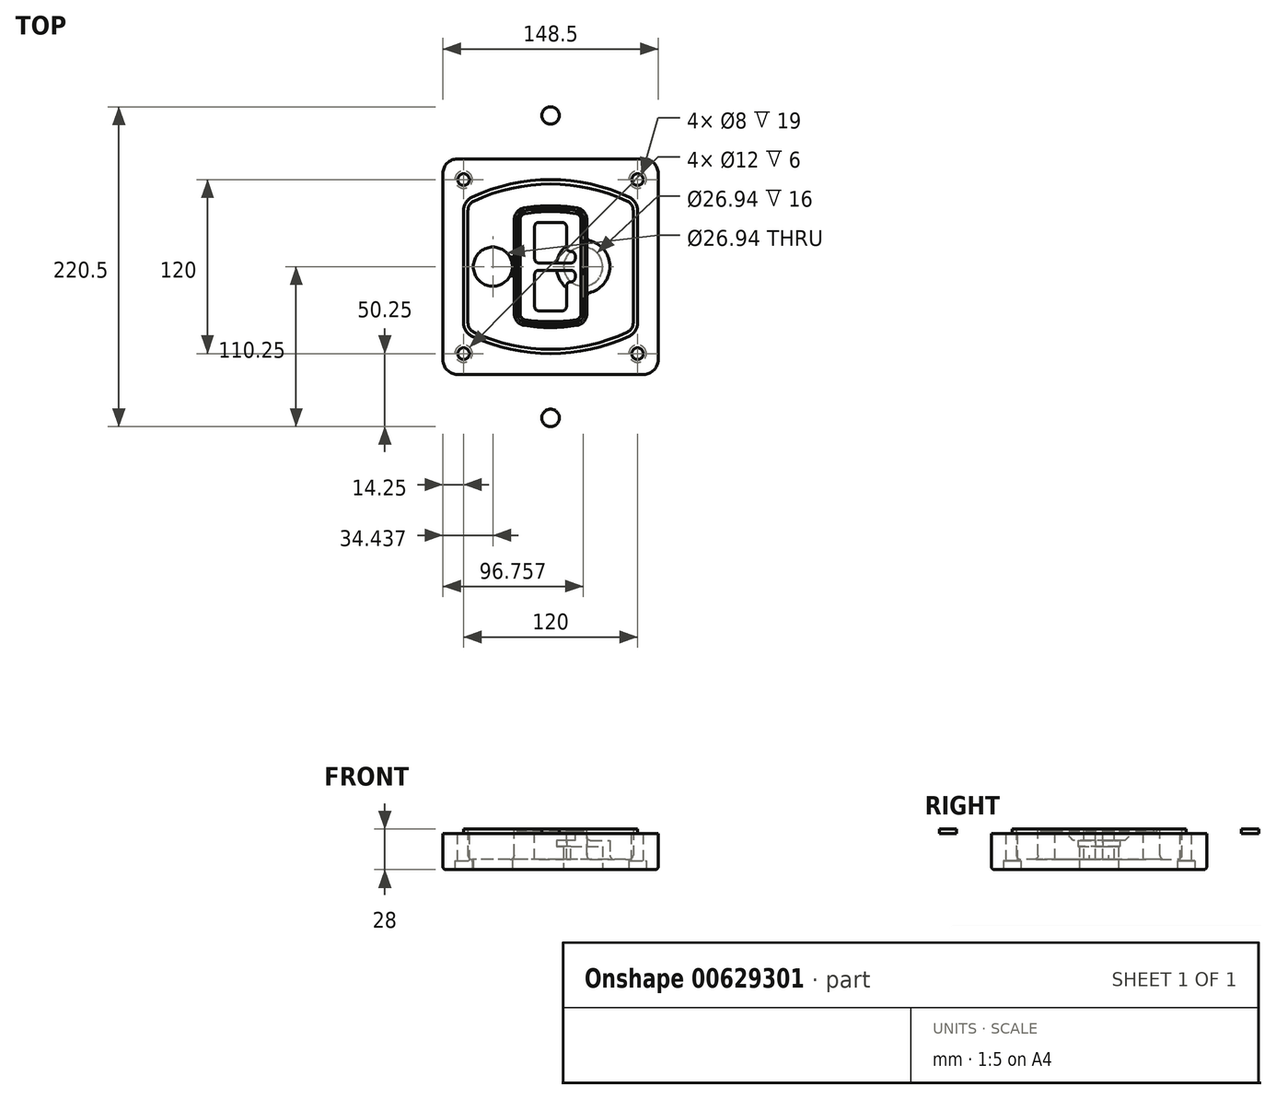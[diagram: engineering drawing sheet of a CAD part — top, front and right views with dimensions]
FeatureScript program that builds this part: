
annotation { "Feature Type Name" : "Feature", "Feature Type Description" : "" }
export const myFeature = defineFeature(function(context is Context, id is Id, definition is map)
    precondition{}
    {
        {
            var Q0;
            Q0=qCreatedBy(makeId("Top.planeOp"),FACE);
            var sketch = newSketch(context, id + "F0", { "sketchPlane" : qUnion([Q0])});
            skPoint(sketch, "E0.rect.middle", {"position": v(0, 0) * mm});
            skLineSegment(sketch, "E1.bottom", {"start": v(-64.25, -74.25) * mm, "end": v(64.25, -74.25) * mm});
            skLineSegment(sketch, "E1.top", {"start": v(-64.25, 74.25) * mm, "end": v(64.25, 74.25) * mm});
            skLineSegment(sketch, "E1.left", {"start": v(-74.25, -64.25) * mm, "end": v(-74.25, 64.25) * mm});
            skLineSegment(sketch, "E1.right", {"start": v(74.25, -64.25) * mm, "end": v(74.25, 64.25) * mm});
            skLineSegment(sketch, "E2", {"start": v(-74.25, 74.25) * mm, "end": v(74.25, -74.25) * mm, "construction": true});
            skLineSegment(sketch, "E3", {"start": v(74.25, 74.25) * mm, "end": v(-74.25, -74.25) * mm, "construction": true});
            skCircle(sketch, "E4", {"center": v(-60, 60) * mm, "radius": 4 * mm});
            skCircle(sketch, "E5", {"center": v(60, 60) * mm, "radius": 4 * mm});
            skCircle(sketch, "E6", {"center": v(60, -60) * mm, "radius": 4 * mm});
            skCircle(sketch, "E7", {"center": v(-60, -60) * mm, "radius": 4 * mm});
            skLineSegment(sketch, "E8", {"start": v(-60, 60) * mm, "end": v(60, 60) * mm, "construction": true});
            skLineSegment(sketch, "E9", {"start": v(60, 60) * mm, "end": v(60, -60) * mm, "construction": true});
            skLineSegment(sketch, "E10", {"start": v(60, -60) * mm, "end": v(-60, -60) * mm, "construction": true});
            skLineSegment(sketch, "E11", {"start": v(-60, -60) * mm, "end": v(-60, 60) * mm, "construction": true});
            skLineSegment(sketch, "E12", {"start": v(-60, 38.83) * mm, "end": v(-60, -38.83) * mm});
            skLineSegment(sketch, "E13", {"start": v(60, 38.83) * mm, "end": v(60, -38.83) * mm});
            skArc(sketch, "E14", {"start": v(54.26, 47.88) * mm, "mid": v(0, 60) * mm, "end": v(-54.26, 47.88) * mm});
            skArc(sketch, "E15", {"start": v(-54.26, -47.88) * mm, "mid": v(0, -60) * mm, "end": v(54.26, -47.88) * mm});
            skLineSegment(sketch, "E16", {"start": v(-60, 0) * mm, "end": v(60, 0) * mm, "construction": true});
            skPoint(sketch, "E17.visualSharp", {"position": v(-60, -45) * mm});
            skArc(sketch, "E17.filletArc", {"start": v(-60, -38.83) * mm, "mid": v(-58.44, -44.2) * mm, "end": v(-54.26, -47.88) * mm});
            skPoint(sketch, "E18.visualSharp", {"position": v(-60, 45) * mm});
            skArc(sketch, "E18.filletArc", {"start": v(-54.26, 47.88) * mm, "mid": v(-58.44, 44.2) * mm, "end": v(-60, 38.83) * mm});
            skPoint(sketch, "E19.visualSharp", {"position": v(60, 45) * mm});
            skArc(sketch, "E19.filletArc", {"start": v(60, 38.83) * mm, "mid": v(58.44, 44.2) * mm, "end": v(54.26, 47.88) * mm});
            skPoint(sketch, "E20.visualSharp", {"position": v(60, -45) * mm});
            skArc(sketch, "E20.filletArc", {"start": v(54.26, -47.88) * mm, "mid": v(58.44, -44.2) * mm, "end": v(60, -38.83) * mm});
            skPoint(sketch, "E21.visualSharp", {"position": v(-74.25, 74.25) * mm});
            skArc(sketch, "E21.filletArc", {"start": v(-64.25, 74.25) * mm, "mid": v(-71.32, 71.32) * mm, "end": v(-74.25, 64.25) * mm});
            skPoint(sketch, "E22.visualSharp", {"position": v(74.25, 74.25) * mm});
            skArc(sketch, "E22.filletArc", {"start": v(74.25, 64.25) * mm, "mid": v(71.32, 71.32) * mm, "end": v(64.25, 74.25) * mm});
            skPoint(sketch, "E23.visualSharp", {"position": v(74.25, -74.25) * mm});
            skArc(sketch, "E23.filletArc", {"start": v(64.25, -74.25) * mm, "mid": v(71.32, -71.32) * mm, "end": v(74.25, -64.25) * mm});
            skPoint(sketch, "E24.visualSharp", {"position": v(-74.25, -74.25) * mm});
            skArc(sketch, "E24.filletArc", {"start": v(-74.25, -64.25) * mm, "mid": v(-71.32, -71.32) * mm, "end": v(-64.25, -74.25) * mm});
            skArc(sketch, "E25.0", {"start": v(57, 38.83) * mm, "mid": v(55.9, 42.58) * mm, "end": v(52.98, 45.17) * mm});
            skLineSegment(sketch, "E25.1", {"start": v(57, 38.83) * mm, "end": v(57, -38.83) * mm});
            skArc(sketch, "E25.2", {"start": v(52.98, -45.17) * mm, "mid": v(55.9, -42.58) * mm, "end": v(57, -38.83) * mm});
            skArc(sketch, "E25.3", {"start": v(-52.98, -45.17) * mm, "mid": v(0, -57) * mm, "end": v(52.98, -45.17) * mm});
            skArc(sketch, "E25.4", {"start": v(-57, -38.83) * mm, "mid": v(-55.9, -42.58) * mm, "end": v(-52.98, -45.17) * mm});
            skArc(sketch, "E25.5", {"start": v(52.98, 45.17) * mm, "mid": v(0, 57) * mm, "end": v(-52.98, 45.17) * mm});
            skLineSegment(sketch, "E25.6", {"start": v(-57, 38.83) * mm, "end": v(-57, -38.83) * mm});
            skArc(sketch, "E25.7", {"start": v(-52.98, 45.17) * mm, "mid": v(-55.9, 42.58) * mm, "end": v(-57, 38.83) * mm});
            skArc(sketch, "E26.0", {"start": v(-55.96, 51.5) * mm, "mid": v(-61.82, 46.33) * mm, "end": v(-64, 38.83) * mm});
            skArc(sketch, "E26.1", {"start": v(55.96, 51.5) * mm, "mid": v(0, 64) * mm, "end": v(-55.96, 51.5) * mm});
            skArc(sketch, "E26.2", {"start": v(64, 38.83) * mm, "mid": v(61.82, 46.33) * mm, "end": v(55.96, 51.5) * mm});
            skLineSegment(sketch, "E26.3", {"start": v(64, 38.83) * mm, "end": v(64, -38.83) * mm});
            skArc(sketch, "E26.4", {"start": v(55.96, -51.5) * mm, "mid": v(61.82, -46.33) * mm, "end": v(64, -38.83) * mm});
            skLineSegment(sketch, "E26.5", {"start": v(-64, 38.83) * mm, "end": v(-64, -38.83) * mm});
            skArc(sketch, "E26.6", {"start": v(-55.96, -51.5) * mm, "mid": v(0, -64) * mm, "end": v(55.96, -51.5) * mm});
            skArc(sketch, "E26.7", {"start": v(-64, -38.83) * mm, "mid": v(-61.82, -46.33) * mm, "end": v(-55.96, -51.5) * mm});
            skSolve(sketch);
        }
        {
            var Q0;
            Q0=makeQuery(id+"F0.imprint","IMPRINT",FACE,{"disambiguationData":[TD([[makeQuery(id+"F0.imprint","IMPRINT",EDGE,{"derivedFrom":sQuery(id+"F0.wireOp",EDGE,"E1.bottom")}),1.0]])]});
            var Q1;
            Q1=makeQuery(id+"F0.imprint","IMPRINT",FACE,{"disambiguationData":[TD([[makeQuery(id+"F0.imprint","IMPRINT",EDGE,{"derivedFrom":sQuery(id+"F0.wireOp",EDGE,"E12")}),1.0]])]});
            var Q2;
            Q2=makeQuery(id+"F0.imprint","IMPRINT",FACE,{"disambiguationData":[TD([[makeQuery(id+"F0.imprint","IMPRINT",EDGE,{"derivedFrom":sQuery(id+"F0.wireOp",EDGE,"E25.0")}),1.0]])]});
            var Q3;
            Q3=makeQuery(id+"F0.imprint","IMPRINT",FACE,{"disambiguationData":[TD([[makeQuery(id+"F0.imprint","IMPRINT",EDGE,{"derivedFrom":sQuery(id+"F0.wireOp",EDGE,"E12")}),-1.0]])]});
            extrude(context, id + "F1", {"entities" : qUnion([Q0, Q1, Q2, Q3]), "oppositeDirection" : true, "depth" : 25 * mm});
        }
        {
            var Q0;
            Q0=makeQuery(id+"F0.imprint","IMPRINT",FACE,{"disambiguationData":[TD([[makeQuery(id+"F0.imprint","IMPRINT",EDGE,{"derivedFrom":sQuery(id+"F0.wireOp",EDGE,"E12")}),1.0]])]});
            extrude(context, id + "F2", {"entities" : qUnion([Q0]), "operationType" : NewBodyOperationType.ADD, "depth" : 3 * mm});
        }
        {
            var Q0;
            Q0=makeQuery(id+"F0.imprint","IMPRINT",FACE,{"disambiguationData":[TD([[makeQuery(id+"F0.imprint","IMPRINT",EDGE,{"derivedFrom":sQuery(id+"F0.wireOp",EDGE,"E25.0")}),1.0]])]});
            extrude(context, id + "F3", {"entities" : qUnion([Q0]), "operationType" : NewBodyOperationType.REMOVE, "oppositeDirection" : true, "depth" : 18 * mm});
        }
        {
            var Q0;
            Q0=makeQuery(id+"F2.opExtrude","CAP_FACE",FACE,{"disambiguationData":[OSD([sQuery(id+"F0.wireOp",EDGE,"E12"),sQuery(id+"F0.wireOp",EDGE,"E13"),sQuery(id+"F0.wireOp",EDGE,"E14"),sQuery(id+"F0.wireOp",EDGE,"E15"),sQuery(id+"F0.wireOp",EDGE,"E17.filletArc"),sQuery(id+"F0.wireOp",EDGE,"E18.filletArc"),sQuery(id+"F0.wireOp",EDGE,"E19.filletArc"),sQuery(id+"F0.wireOp",EDGE,"E20.filletArc"),sQuery(id+"F0.wireOp",EDGE,"E25.0"),sQuery(id+"F0.wireOp",EDGE,"E25.1"),sQuery(id+"F0.wireOp",EDGE,"E25.2"),sQuery(id+"F0.wireOp",EDGE,"E25.3"),sQuery(id+"F0.wireOp",EDGE,"E25.4"),sQuery(id+"F0.wireOp",EDGE,"E25.5"),sQuery(id+"F0.wireOp",EDGE,"E25.6"),sQuery(id+"F0.wireOp",EDGE,"E25.7")])],"isStart":false});
            var sketch = newSketch(context, id + "F4", { "sketchPlane" : qUnion([Q0])});
            skArc(sketch, "E27.0", {"start": v(-18.34, -40.45) * mm, "mid": v(0, -42) * mm, "end": v(18.34, -40.45) * mm});
            skArc(sketch, "E28.0", {"start": v(18.34, 40.45) * mm, "mid": v(0, 42) * mm, "end": v(-18.34, 40.45) * mm});
            skLineSegment(sketch, "E29", {"start": v(-25, 32.57) * mm, "end": v(-25, -32.57) * mm});
            skLineSegment(sketch, "E30", {"start": v(25, 32.57) * mm, "end": v(25, -32.57) * mm});
            skLineSegment(sketch, "E31", {"start": v(-25, 39.1) * mm, "end": v(25, 39.1) * mm, "construction": true});
            skLineSegment(sketch, "E32", {"start": v(-25, -39.1) * mm, "end": v(25, -39.1) * mm, "construction": true});
            skPoint(sketch, "E33.visualSharp", {"position": v(-25, 39.1) * mm});
            skArc(sketch, "E33.filletArc", {"start": v(-18.34, 40.45) * mm, "mid": v(-23.11, 37.73) * mm, "end": v(-25, 32.57) * mm});
            skPoint(sketch, "E34.visualSharp", {"position": v(25, 39.1) * mm});
            skArc(sketch, "E34.filletArc", {"start": v(25, 32.57) * mm, "mid": v(23.11, 37.73) * mm, "end": v(18.34, 40.45) * mm});
            skPoint(sketch, "E35.visualSharp", {"position": v(25, -39.1) * mm});
            skArc(sketch, "E35.filletArc", {"start": v(18.34, -40.45) * mm, "mid": v(23.11, -37.73) * mm, "end": v(25, -32.57) * mm});
            skPoint(sketch, "E36.visualSharp", {"position": v(-25, -39.1) * mm});
            skArc(sketch, "E36.filletArc", {"start": v(-25, -32.57) * mm, "mid": v(-23.11, -37.73) * mm, "end": v(-18.34, -40.45) * mm});
            skArc(sketch, "E37.0", {"start": v(52.98, 45.17) * mm, "mid": v(0, 57) * mm, "end": v(-52.98, 45.17) * mm});
            skArc(sketch, "E37.1", {"start": v(-52.98, 45.17) * mm, "mid": v(-55.9, 42.58) * mm, "end": v(-57, 38.83) * mm});
            skLineSegment(sketch, "E37.2", {"start": v(-57, 38.83) * mm, "end": v(-57, -38.83) * mm});
            skArc(sketch, "E37.3", {"start": v(-57, -38.83) * mm, "mid": v(-55.9, -42.58) * mm, "end": v(-52.98, -45.17) * mm});
            skArc(sketch, "E37.4", {"start": v(-52.98, -45.17) * mm, "mid": v(0, -57) * mm, "end": v(52.98, -45.17) * mm});
            skArc(sketch, "E37.5", {"start": v(52.98, -45.17) * mm, "mid": v(55.9, -42.58) * mm, "end": v(57, -38.83) * mm});
            skLineSegment(sketch, "E37.6", {"start": v(57, 38.83) * mm, "end": v(57, -38.83) * mm});
            skArc(sketch, "E37.7", {"start": v(57, 38.83) * mm, "mid": v(55.9, 42.58) * mm, "end": v(52.98, 45.17) * mm});
            skLineSegment(sketch, "E38.0", {"start": v(23, 32.57) * mm, "end": v(23, -32.57) * mm});
            skArc(sketch, "E38.1", {"start": v(18, -38.48) * mm, "mid": v(21.58, -36.44) * mm, "end": v(23, -32.57) * mm});
            skArc(sketch, "E38.2", {"start": v(-18, -38.48) * mm, "mid": v(0, -40) * mm, "end": v(18, -38.48) * mm});
            skArc(sketch, "E38.3", {"start": v(-23, -32.57) * mm, "mid": v(-21.58, -36.44) * mm, "end": v(-18, -38.48) * mm});
            skLineSegment(sketch, "E38.4", {"start": v(-23, 32.57) * mm, "end": v(-23, -32.57) * mm});
            skArc(sketch, "E38.5", {"start": v(23, 32.57) * mm, "mid": v(21.58, 36.44) * mm, "end": v(18, 38.48) * mm});
            skArc(sketch, "E38.6", {"start": v(-18, 38.48) * mm, "mid": v(-21.58, 36.44) * mm, "end": v(-23, 32.57) * mm});
            skArc(sketch, "E38.7", {"start": v(18, 38.48) * mm, "mid": v(0, 40) * mm, "end": v(-18, 38.48) * mm});
            skArc(sketch, "E39.0", {"start": v(21, 32.57) * mm, "mid": v(20.06, 35.15) * mm, "end": v(17.67, 36.5) * mm});
            skLineSegment(sketch, "E39.1", {"start": v(21, 32.57) * mm, "end": v(21, -32.57) * mm});
            skArc(sketch, "E39.2", {"start": v(17.67, -36.5) * mm, "mid": v(20.06, -35.15) * mm, "end": v(21, -32.57) * mm});
            skArc(sketch, "E39.3", {"start": v(-17.67, -36.5) * mm, "mid": v(0, -38) * mm, "end": v(17.67, -36.5) * mm});
            skArc(sketch, "E39.4", {"start": v(-21, -32.57) * mm, "mid": v(-20.06, -35.15) * mm, "end": v(-17.67, -36.5) * mm});
            skArc(sketch, "E39.5", {"start": v(17.67, 36.5) * mm, "mid": v(0, 38) * mm, "end": v(-17.67, 36.5) * mm});
            skLineSegment(sketch, "E39.6", {"start": v(-21, 32.57) * mm, "end": v(-21, -32.57) * mm});
            skArc(sketch, "E39.7", {"start": v(-17.67, 36.5) * mm, "mid": v(-20.06, 35.15) * mm, "end": v(-21, 32.57) * mm});
            skLineSegment(sketch, "E40", {"start": v(-25, 0) * mm, "end": v(25, 0) * mm, "construction": true});
            skLineSegment(sketch, "E41", {"start": v(-11, 5.5) * mm, "end": v(-11, 27.5) * mm});
            skLineSegment(sketch, "E42", {"start": v(-8, 30.5) * mm, "end": v(8, 30.5) * mm});
            skLineSegment(sketch, "E43", {"start": v(11, 27.5) * mm, "end": v(11, 13.5) * mm});
            skLineSegment(sketch, "E44", {"start": v(14, 10.5) * mm, "end": v(14, 10.5) * mm});
            skLineSegment(sketch, "E45", {"start": v(17, 7.5) * mm, "end": v(17, 5.5) * mm});
            skLineSegment(sketch, "E46", {"start": v(14, 2.5) * mm, "end": v(-8, 2.5) * mm});
            skPoint(sketch, "E47.visualSharp", {"position": v(-11, 30.5) * mm});
            skArc(sketch, "E47.filletArc", {"start": v(-8, 30.5) * mm, "mid": v(-10.12, 29.62) * mm, "end": v(-11, 27.5) * mm});
            skPoint(sketch, "E48.visualSharp", {"position": v(11, 30.5) * mm});
            skArc(sketch, "E48.filletArc", {"start": v(11, 27.5) * mm, "mid": v(10.12, 29.62) * mm, "end": v(8, 30.5) * mm});
            skPoint(sketch, "E49.visualSharp", {"position": v(11, 10.5) * mm});
            skArc(sketch, "E49.filletArc", {"start": v(11, 13.5) * mm, "mid": v(11.88, 11.38) * mm, "end": v(14, 10.5) * mm});
            skPoint(sketch, "E50.visualSharp", {"position": v(17, 10.5) * mm});
            skArc(sketch, "E50.filletArc", {"start": v(17, 7.5) * mm, "mid": v(16.12, 9.62) * mm, "end": v(14, 10.5) * mm});
            skPoint(sketch, "E51.visualSharp", {"position": v(17, 2.5) * mm});
            skArc(sketch, "E51.filletArc", {"start": v(14, 2.5) * mm, "mid": v(16.12, 3.38) * mm, "end": v(17, 5.5) * mm});
            skPoint(sketch, "E52.visualSharp", {"position": v(-11, 2.5) * mm});
            skArc(sketch, "E52.filletArc", {"start": v(-11, 5.5) * mm, "mid": v(-10.12, 3.38) * mm, "end": v(-8, 2.5) * mm});
            skLineSegment(sketch, "E53.0.MirrorCS", {"start": v(14, -2.5) * mm, "end": v(-8, -2.5) * mm});
            skArc(sketch, "E54.0.MirrorCS", {"start": v(-11, -5.5) * mm, "mid": v(-10.12, -3.38) * mm, "end": v(-8, -2.5) * mm});
            skLineSegment(sketch, "E55.0.MirrorCS", {"start": v(-11, -5.5) * mm, "end": v(-11, -27.5) * mm});
            skArc(sketch, "E56.0.MirrorCS", {"start": v(-8, -30.5) * mm, "mid": v(-10.12, -29.62) * mm, "end": v(-11, -27.5) * mm});
            skLineSegment(sketch, "E57.0.MirrorCS", {"start": v(-8, -30.5) * mm, "end": v(8, -30.5) * mm});
            skArc(sketch, "E58.0.MirrorCS", {"start": v(11, -27.5) * mm, "mid": v(10.12, -29.62) * mm, "end": v(8, -30.5) * mm});
            skLineSegment(sketch, "E59.0.MirrorCS", {"start": v(11, -27.5) * mm, "end": v(11, -13.5) * mm});
            skArc(sketch, "E60.0.MirrorCS", {"start": v(11, -13.5) * mm, "mid": v(11.88, -11.38) * mm, "end": v(14, -10.5) * mm});
            skArc(sketch, "E61.0.MirrorCS", {"start": v(17, -7.5) * mm, "mid": v(16.12, -9.62) * mm, "end": v(14, -10.5) * mm});
            skLineSegment(sketch, "E62.0.MirrorCS", {"start": v(17, -7.5) * mm, "end": v(17, -5.5) * mm});
            skArc(sketch, "E63.0.MirrorCS", {"start": v(14, -2.5) * mm, "mid": v(16.12, -3.38) * mm, "end": v(17, -5.5) * mm});
            skSolve(sketch);
        }
        {
            var Q0;
            Q0=makeQuery(id+"F4.imprint","IMPRINT",FACE,{"disambiguationData":[TD([[makeQuery(id+"F4.imprint","IMPRINT",EDGE,{"derivedFrom":sQuery(id+"F4.wireOp",EDGE,"E27.0")}),1.0]])]});
            var Q1;
            Q1=makeQuery(id+"F4.imprint","IMPRINT",FACE,{"disambiguationData":[TD([[makeQuery(id+"F4.imprint","IMPRINT",EDGE,{"derivedFrom":sQuery(id+"F4.wireOp",EDGE,"E38.0")}),-1.0]])]});
            var Q2;
            Q2=makeQuery(id+"F4.imprint","IMPRINT",FACE,{"disambiguationData":[TD([[makeQuery(id+"F4.imprint","IMPRINT",EDGE,{"derivedFrom":sQuery(id+"F4.wireOp",EDGE,"E39.0")}),1.0]])]});
            extrude(context, id + "F5", {"entities" : qUnion([Q0, Q1, Q2]), "operationType" : NewBodyOperationType.ADD, "endBound" : BoundingType.UP_TO_NEXT, "oppositeDirection" : true, "depth" : 25 * mm});
        }
        {
            var Q0;
            Q0=makeQuery(id+"F4.imprint","IMPRINT",FACE,{"disambiguationData":[TD([[makeQuery(id+"F4.imprint","IMPRINT",EDGE,{"derivedFrom":sQuery(id+"F4.wireOp",EDGE,"E38.0")}),-1.0]])]});
            extrude(context, id + "F6", {"entities" : qUnion([Q0]), "operationType" : NewBodyOperationType.REMOVE, "oppositeDirection" : true, "depth" : 2 * mm});
        }
        {
            var Q0;
            Q0=makeQuery(id+"F1.opExtrude","CAP_FACE",FACE,{"disambiguationData":[OSD([sQuery(id+"F0.wireOp",EDGE,"E1.bottom"),sQuery(id+"F0.wireOp",EDGE,"E1.top"),sQuery(id+"F0.wireOp",EDGE,"E1.left"),sQuery(id+"F0.wireOp",EDGE,"E1.right"),sQuery(id+"F0.wireOp",EDGE,"E4"),sQuery(id+"F0.wireOp",EDGE,"E5"),sQuery(id+"F0.wireOp",EDGE,"E6"),sQuery(id+"F0.wireOp",EDGE,"E7"),sQuery(id+"F0.wireOp",EDGE,"E21.filletArc"),sQuery(id+"F0.wireOp",EDGE,"E22.filletArc"),sQuery(id+"F0.wireOp",EDGE,"E23.filletArc"),sQuery(id+"F0.wireOp",EDGE,"E24.filletArc")])],"isStart":false});
            var sketch = newSketch(context, id + "F7", { "sketchPlane" : qUnion([Q0])});
            skCircle(sketch, "E64", {"center": v(22.5, 0) * mm, "radius": 13.47 * mm});
            skCircle(sketch, "E65", {"center": v(-39.81, 0) * mm, "radius": 13.47 * mm});
            skLineSegment(sketch, "E66", {"start": v(74.25, 0) * mm, "end": v(-74.25, 0) * mm});
            skCircle(sketch, "E67", {"center": v(22.5, 0) * mm, "radius": 18.47 * mm});
            skCircle(sketch, "E68", {"center": v(60, -60) * mm, "radius": 6 * mm});
            skCircle(sketch, "E69", {"center": v(-60, -60) * mm, "radius": 6 * mm});
            skCircle(sketch, "E70", {"center": v(-60, 60) * mm, "radius": 6 * mm});
            skCircle(sketch, "E71", {"center": v(60, 60) * mm, "radius": 6 * mm});
            skSolve(sketch);
        }
        {
            var Q0;
            {var subQ1=sQuery(id+"F7.wireOp",EDGE,"E66");var subQ4=sQuery(id+"F7.wireOp",EDGE,"E64");var subQ6=makeQuery(id+"F7.imprint","INTERSECT",VERTEX,{"disambiguationData":[OD(0.0)],"derivedFrom":[subQ4,subQ1]});Q0=makeQuery(id+"F7.imprint","IMPRINT",FACE,{"disambiguationData":[TD([[makeQuery(id+"F7.imprint","IMPRINT",EDGE,{"disambiguationData":[TD([[subQ6,-1.0]])],"derivedFrom":subQ4}),-1.0]])]});}
            var Q1;
            {var subQ0=sQuery(id+"F7.wireOp",EDGE,"E66");var subQ1=sQuery(id+"F7.wireOp",EDGE,"E64");var subQ3=makeQuery(id+"F7.imprint","INTERSECT",VERTEX,{"disambiguationData":[OD(0.0)],"derivedFrom":[subQ1,subQ0]});Q1=makeQuery(id+"F7.imprint","IMPRINT",FACE,{"disambiguationData":[TD([[makeQuery(id+"F7.imprint","IMPRINT",EDGE,{"disambiguationData":[TD([[subQ3,-1.0]])],"derivedFrom":subQ1}),1.0]])]});}
            var Q2;
            {var subQ0=sQuery(id+"F7.wireOp",EDGE,"E66");var subQ1=sQuery(id+"F7.wireOp",EDGE,"E64");var subQ3=makeQuery(id+"F7.imprint","INTERSECT",VERTEX,{"disambiguationData":[OD(0.0)],"derivedFrom":[subQ1,subQ0]});Q2=makeQuery(id+"F7.imprint","IMPRINT",FACE,{"disambiguationData":[TD([[makeQuery(id+"F7.imprint","IMPRINT",EDGE,{"disambiguationData":[TD([[subQ3,1.0]])],"derivedFrom":subQ1}),1.0]])]});}
            var Q3;
            {var subQ1=sQuery(id+"F7.wireOp",EDGE,"E66");var subQ4=sQuery(id+"F7.wireOp",EDGE,"E64");var subQ6=makeQuery(id+"F7.imprint","INTERSECT",VERTEX,{"disambiguationData":[OD(0.0)],"derivedFrom":[subQ4,subQ1]});Q3=makeQuery(id+"F7.imprint","IMPRINT",FACE,{"disambiguationData":[TD([[makeQuery(id+"F7.imprint","IMPRINT",EDGE,{"disambiguationData":[TD([[subQ6,1.0]])],"derivedFrom":subQ4}),-1.0]])]});}
            extrude(context, id + "F8", {"entities" : qUnion([Q0, Q1, Q2, Q3]), "operationType" : NewBodyOperationType.ADD, "oppositeDirection" : true, "depth" : 20 * mm});
        }
        {
            var Q0;
            {var subQ0=sQuery(id+"F7.wireOp",EDGE,"E66");var subQ1=sQuery(id+"F7.wireOp",EDGE,"E64");var subQ3=makeQuery(id+"F7.imprint","INTERSECT",VERTEX,{"disambiguationData":[OD(0.0)],"derivedFrom":[subQ1,subQ0]});Q0=makeQuery(id+"F7.imprint","IMPRINT",FACE,{"disambiguationData":[TD([[makeQuery(id+"F7.imprint","IMPRINT",EDGE,{"disambiguationData":[TD([[subQ3,-1.0]])],"derivedFrom":subQ1}),1.0]])]});}
            var Q1;
            {var subQ0=sQuery(id+"F7.wireOp",EDGE,"E66");var subQ1=sQuery(id+"F7.wireOp",EDGE,"E64");var subQ3=makeQuery(id+"F7.imprint","INTERSECT",VERTEX,{"disambiguationData":[OD(0.0)],"derivedFrom":[subQ1,subQ0]});Q1=makeQuery(id+"F7.imprint","IMPRINT",FACE,{"disambiguationData":[TD([[makeQuery(id+"F7.imprint","IMPRINT",EDGE,{"disambiguationData":[TD([[subQ3,1.0]])],"derivedFrom":subQ1}),1.0]])]});}
            extrude(context, id + "F9", {"entities" : qUnion([Q0, Q1]), "operationType" : NewBodyOperationType.REMOVE, "oppositeDirection" : true, "depth" : 16 * mm});
        }
        {
            var Q0;
            {var subQ0=sQuery(id+"F7.wireOp",EDGE,"E66");var subQ1=sQuery(id+"F7.wireOp",EDGE,"E65");var subQ3=makeQuery(id+"F7.imprint","INTERSECT",VERTEX,{"disambiguationData":[OD(0.0)],"derivedFrom":[subQ1,subQ0]});Q0=makeQuery(id+"F7.imprint","IMPRINT",FACE,{"disambiguationData":[TD([[makeQuery(id+"F7.imprint","IMPRINT",EDGE,{"disambiguationData":[TD([[subQ3,-1.0]])],"derivedFrom":subQ1}),1.0]])]});}
            var Q1;
            {var subQ0=sQuery(id+"F7.wireOp",EDGE,"E66");var subQ1=sQuery(id+"F7.wireOp",EDGE,"E65");var subQ3=makeQuery(id+"F7.imprint","INTERSECT",VERTEX,{"disambiguationData":[OD(0.0)],"derivedFrom":[subQ1,subQ0]});Q1=makeQuery(id+"F7.imprint","IMPRINT",FACE,{"disambiguationData":[TD([[makeQuery(id+"F7.imprint","IMPRINT",EDGE,{"disambiguationData":[TD([[subQ3,1.0]])],"derivedFrom":subQ1}),1.0]])]});}
            extrude(context, id + "F10", {"entities" : qUnion([Q0, Q1]), "operationType" : NewBodyOperationType.REMOVE, "oppositeDirection" : true, "depth" : 25 * mm});
        }
        {
            var Q0;
            Q0=makeQuery(id+"F7.imprint","IMPRINT",FACE,{"disambiguationData":[TD([[makeQuery(id+"F7.imprint","IMPRINT",EDGE,{"derivedFrom":sQuery(id+"F7.wireOp",EDGE,"E68")}),1.0]])]});
            var Q1;
            Q1=makeQuery(id+"F7.imprint","IMPRINT",FACE,{"disambiguationData":[TD([[makeQuery(id+"F7.imprint","IMPRINT",EDGE,{"derivedFrom":makeQuery(id+"F1.opExtrude","CAP_EDGE",EDGE,{"disambiguationData":[OSD([sQuery(id+"F0.wireOp",EDGE,"E5")])],"isStart":false})}),-1.0]])]});
            var Q2;
            Q2=makeQuery(id+"F7.imprint","IMPRINT",FACE,{"disambiguationData":[TD([[makeQuery(id+"F7.imprint","IMPRINT",EDGE,{"derivedFrom":sQuery(id+"F7.wireOp",EDGE,"E69")}),1.0]])]});
            var Q3;
            Q3=makeQuery(id+"F7.imprint","IMPRINT",FACE,{"disambiguationData":[TD([[makeQuery(id+"F7.imprint","IMPRINT",EDGE,{"derivedFrom":makeQuery(id+"F1.opExtrude","CAP_EDGE",EDGE,{"disambiguationData":[OSD([sQuery(id+"F0.wireOp",EDGE,"E4")])],"isStart":false})}),-1.0]])]});
            var Q4;
            Q4=makeQuery(id+"F7.imprint","IMPRINT",FACE,{"disambiguationData":[TD([[makeQuery(id+"F7.imprint","IMPRINT",EDGE,{"derivedFrom":sQuery(id+"F7.wireOp",EDGE,"E70")}),1.0]])]});
            var Q5;
            Q5=makeQuery(id+"F7.imprint","IMPRINT",FACE,{"disambiguationData":[TD([[makeQuery(id+"F7.imprint","IMPRINT",EDGE,{"derivedFrom":makeQuery(id+"F1.opExtrude","CAP_EDGE",EDGE,{"disambiguationData":[OSD([sQuery(id+"F0.wireOp",EDGE,"E7")])],"isStart":false})}),-1.0]])]});
            var Q6;
            Q6=makeQuery(id+"F7.imprint","IMPRINT",FACE,{"disambiguationData":[TD([[makeQuery(id+"F7.imprint","IMPRINT",EDGE,{"derivedFrom":sQuery(id+"F7.wireOp",EDGE,"E71")}),1.0]])]});
            var Q7;
            Q7=makeQuery(id+"F7.imprint","IMPRINT",FACE,{"disambiguationData":[TD([[makeQuery(id+"F7.imprint","IMPRINT",EDGE,{"derivedFrom":makeQuery(id+"F1.opExtrude","CAP_EDGE",EDGE,{"disambiguationData":[OSD([sQuery(id+"F0.wireOp",EDGE,"E6")])],"isStart":false})}),-1.0]])]});
            extrude(context, id + "F11", {"entities" : qUnion([Q0, Q1, Q2, Q3, Q4, Q5, Q6, Q7]), "operationType" : NewBodyOperationType.REMOVE, "oppositeDirection" : true, "depth" : 6 * mm});
        }
        {
            var Q0;
            Q0=makeQuery(id+"F9.boolean.opBoolean","COPY",FACE,{"derivedFrom":makeQuery(id+"F9.opExtrude","CAP_FACE",FACE,{"disambiguationData":[OSD([sQuery(id+"F7.wireOp",EDGE,"E64")])],"isStart":false})});
            var sketch = newSketch(context, id + "F12", { "sketchPlane" : qUnion([Q0])});
            skArc(sketch, "E72.0", {"start": v(11, 14.45) * mm, "mid": v(6.45, 9.13) * mm, "end": v(4.2, 2.5) * mm});
            skArc(sketch, "E72.1", {"start": v(4.2, -2.5) * mm, "mid": v(6.45, -9.13) * mm, "end": v(11, -14.45) * mm});
            skLineSegment(sketch, "E73", {"start": v(4.2, -2.5) * mm, "end": v(14, -2.5) * mm});
            skLineSegment(sketch, "E74.0", {"start": v(14, 2.5) * mm, "end": v(4.2, 2.5) * mm});
            skArc(sketch, "E74.1", {"start": v(14, 2.5) * mm, "mid": v(16.12, 3.38) * mm, "end": v(17, 5.5) * mm});
            skLineSegment(sketch, "E74.2", {"start": v(17, 7.5) * mm, "end": v(17, 5.5) * mm});
            skArc(sketch, "E74.3", {"start": v(17, 7.5) * mm, "mid": v(16.12, 9.62) * mm, "end": v(14, 10.5) * mm});
            skArc(sketch, "E74.4", {"start": v(11, 13.5) * mm, "mid": v(11.88, 11.38) * mm, "end": v(14, 10.5) * mm});
            skLineSegment(sketch, "E74.5", {"start": v(11, 14.45) * mm, "end": v(11, 13.5) * mm});
            skLineSegment(sketch, "E74.7", {"start": v(14, -2.5) * mm, "end": v(4.2, -2.5) * mm});
            skArc(sketch, "E74.8", {"start": v(14, -2.5) * mm, "mid": v(16.12, -3.38) * mm, "end": v(17, -5.5) * mm});
            skLineSegment(sketch, "E74.9", {"start": v(17, -7.5) * mm, "end": v(17, -5.5) * mm});
            skArc(sketch, "E74.10", {"start": v(17, -7.5) * mm, "mid": v(16.12, -9.62) * mm, "end": v(14, -10.5) * mm});
            skArc(sketch, "E74.11", {"start": v(11, -13.5) * mm, "mid": v(11.88, -11.38) * mm, "end": v(14, -10.5) * mm});
            skLineSegment(sketch, "E74.12", {"start": v(11, -14.45) * mm, "end": v(11, -13.5) * mm});
            skPoint(sketch, "E75.orphan", {"position": v(11, -27.5) * mm});
            skPoint(sketch, "E76.orphan", {"position": v(-8, -2.5) * mm});
            skPoint(sketch, "E77.orphan", {"position": v(-8, 2.5) * mm});
            skPoint(sketch, "E78.orphan", {"position": v(11, 27.5) * mm});
            skSolve(sketch);
        }
        {
            var Q0;
            {var subQ7=sQuery(id+"F12.wireOp",EDGE,"E72.0");var subQ14=sQuery(id+"F12.wireOp",EDGE,"E72.1");var subQ16=sQuery(id+"F12.wireOp",EDGE,"E74.1");var subQ18=sQuery(id+"F12.wireOp",EDGE,"E74.8");Q0=qUnion([makeQuery(id+"F12.imprint","IMPRINT",FACE,{"disambiguationData":[TD([[makeQuery(id+"F12.imprint","IMPRINT",EDGE,{"derivedFrom":subQ7}),1.0]])]}),makeQuery(id+"F12.imprint","IMPRINT",FACE,{"disambiguationData":[TD([[makeQuery(id+"F12.imprint","IMPRINT",EDGE,{"derivedFrom":subQ14}),1.0]])]}),makeQuery(id+"F12.imprint","IMPRINT",FACE,{"disambiguationData":[TD([[makeQuery(id+"F12.imprint","IMPRINT",EDGE,{"derivedFrom":subQ16}),1.0]])]}),makeQuery(id+"F12.imprint","IMPRINT",FACE,{"disambiguationData":[TD([[makeQuery(id+"F12.imprint","IMPRINT",EDGE,{"derivedFrom":subQ18}),-1.0]])]})]);}
            var Q1;
            Q1=makeQuery(id+"F5.boolean.opBoolean","SPLIT",FACE,{"disambiguationData":[TD([makeQuery(id+"F5.opExtrude","SWEPT_FACE",FACE,{"disambiguationData":[OSD([sQuery(id+"F4.wireOp",EDGE,"E41")])]})])],"derivedFrom":makeQuery(id+"F3.boolean.opBoolean","COPY",FACE,{"derivedFrom":makeQuery(id+"F3.opExtrude","CAP_FACE",FACE,{"disambiguationData":[OSD([sQuery(id+"F0.wireOp",EDGE,"E25.0"),sQuery(id+"F0.wireOp",EDGE,"E25.1"),sQuery(id+"F0.wireOp",EDGE,"E25.2"),sQuery(id+"F0.wireOp",EDGE,"E25.3"),sQuery(id+"F0.wireOp",EDGE,"E25.4"),sQuery(id+"F0.wireOp",EDGE,"E25.5"),sQuery(id+"F0.wireOp",EDGE,"E25.6"),sQuery(id+"F0.wireOp",EDGE,"E25.7")])],"isStart":false})})});
            extrude(context, id + "F13", {"entities" : qUnion([Q0]), "operationType" : NewBodyOperationType.REMOVE, "endBound" : BoundingType.UP_TO_SURFACE, "endBoundEntityFace" : qUnion([Q1]), "depth" : 25 * mm});
        }
        {
            var Q0;
            Q0=makeQuery(id+"F3.boolean.opBoolean","COPY",EDGE,{"derivedFrom":makeQuery(id+"F3.opExtrude","CAP_EDGE",EDGE,{"disambiguationData":[OSD([sQuery(id+"F0.wireOp",EDGE,"E25.6")])],"isStart":false})});
            var Q1;
            Q1=makeQuery(id+"F8.boolean.opBoolean","INTERSECT",EDGE,{"derivedFrom":[makeQuery(id+"F5.opExtrude","SWEPT_FACE",FACE,{"disambiguationData":[OSD([sQuery(id+"F4.wireOp",EDGE,"E30")])]}),makeQuery(id+"F8.opExtrude","CAP_FACE",FACE,{"disambiguationData":[OSD([sQuery(id+"F7.wireOp",EDGE,"E67")])],"isStart":false})]});
            var Q2;
            Q2=makeQuery(id+"F8.boolean.opBoolean","INTERSECT",EDGE,{"disambiguationData":[OD(1.0)],"derivedFrom":[makeQuery(id+"F5.opExtrude","SWEPT_FACE",FACE,{"disambiguationData":[OSD([sQuery(id+"F4.wireOp",EDGE,"E30")])]}),makeQuery(id+"F8.opExtrude","SWEPT_FACE",FACE,{"disambiguationData":[OSD([sQuery(id+"F7.wireOp",EDGE,"E67")])]})]});
            var Q3;
            {var subQ0=sQuery(id+"F4.wireOp",EDGE,"E30");Q3=makeQuery(id+"F8.boolean.opBoolean","SPLIT",EDGE,{"disambiguationData":[TD([makeQuery(id+"F5.opExtrude","SWEPT_FACE",FACE,{"disambiguationData":[OSD([sQuery(id+"F4.wireOp",EDGE,"E35.filletArc")])]})])],"derivedFrom":makeQuery(id+"F5.opExtrude","CAP_EDGE",EDGE,{"disambiguationData":[OSD([subQ0])],"isStart":false})});}
            var Q4;
            {var subQ0=sQuery(id+"F0.wireOp",EDGE,"E25.7");var subQ1=sQuery(id+"F0.wireOp",EDGE,"E25.1");var subQ2=sQuery(id+"F0.wireOp",EDGE,"E25.6");var subQ3=sQuery(id+"F0.wireOp",EDGE,"E25.5");var subQ4=sQuery(id+"F0.wireOp",EDGE,"E25.4");var subQ5=sQuery(id+"F0.wireOp",EDGE,"E25.0");var subQ6=sQuery(id+"F0.wireOp",EDGE,"E25.2");var subQ7=sQuery(id+"F0.wireOp",EDGE,"E25.3");Q4=makeQuery(id+"F8.boolean.opBoolean","INTERSECT",EDGE,{"derivedFrom":[makeQuery(id+"F5.boolean.opBoolean","SPLIT",FACE,{"disambiguationData":[TD([makeQuery(id+"F2.opExtrude","SWEPT_FACE",FACE,{"disambiguationData":[OSD([subQ5])]})])],"derivedFrom":makeQuery(id+"F3.boolean.opBoolean","COPY",FACE,{"derivedFrom":makeQuery(id+"F3.opExtrude","CAP_FACE",FACE,{"disambiguationData":[OSD([subQ5,subQ1,subQ6,subQ7,subQ4,subQ3,subQ2,subQ0])],"isStart":false})})}),makeQuery(id+"F8.opExtrude","SWEPT_FACE",FACE,{"disambiguationData":[OSD([sQuery(id+"F7.wireOp",EDGE,"E67")])]})]});}
            var Q5;
            Q5=makeQuery(id+"F8.boolean.opBoolean","INTERSECT",EDGE,{"disambiguationData":[OD(0.0)],"derivedFrom":[makeQuery(id+"F5.opExtrude","SWEPT_FACE",FACE,{"disambiguationData":[OSD([sQuery(id+"F4.wireOp",EDGE,"E30")])]}),makeQuery(id+"F8.opExtrude","SWEPT_FACE",FACE,{"disambiguationData":[OSD([sQuery(id+"F7.wireOp",EDGE,"E67")])]})]});
            fillet(context, id + "F14", {"entities" : qUnion([Q0, Q1, Q2, Q3, Q4, Q5]), "radius" : 3 * mm, "tangentPropagation" : true, "allowEdgeOverflow" : false});
        }
        {
            var Q0;
            Q0=makeQuery(id+"F1.opExtrude","CAP_EDGE",EDGE,{"disambiguationData":[OSD([sQuery(id+"F0.wireOp",EDGE,"E1.bottom")])],"isStart":false});
            fillet(context, id + "F15", {"entities" : qUnion([Q0]), "radius" : 2 * mm, "tangentPropagation" : true, "allowEdgeOverflow" : false});
        }
        {
            var Q0;
            {var subQ0=sQuery(id+"F0.wireOp",EDGE,"E21.filletArc");var subQ1=sQuery(id+"F0.wireOp",EDGE,"E7");var subQ2=sQuery(id+"F0.wireOp",EDGE,"E6");var subQ3=sQuery(id+"F0.wireOp",EDGE,"E5");var subQ4=sQuery(id+"F0.wireOp",EDGE,"E4");var subQ5=sQuery(id+"F0.wireOp",EDGE,"E22.filletArc");var subQ6=sQuery(id+"F0.wireOp",EDGE,"E1.bottom");var subQ7=sQuery(id+"F0.wireOp",EDGE,"E1.right");var subQ8=sQuery(id+"F0.wireOp",EDGE,"E1.top");var subQ9=sQuery(id+"F0.wireOp",EDGE,"E1.left");var subQ10=sQuery(id+"F0.wireOp",EDGE,"E23.filletArc");var subQ11=sQuery(id+"F0.wireOp",EDGE,"E24.filletArc");Q0=makeQuery(id+"F2.boolean.opBoolean","SPLIT",FACE,{"disambiguationData":[TD([makeQuery(id+"F1.opExtrude","SWEPT_FACE",FACE,{"disambiguationData":[OSD([subQ6])]})])],"derivedFrom":makeQuery(id+"F1.opExtrude","CAP_FACE",FACE,{"disambiguationData":[OSD([subQ6,subQ8,subQ9,subQ7,subQ4,subQ3,subQ2,subQ1,subQ0,subQ5,subQ10,subQ11])],"isStart":true})});}
            var sketch = newSketch(context, id + "F16", { "sketchPlane" : qUnion([Q0])});
            skCircle(sketch, "E79", {"center": v(0, 104.25) * mm, "radius": 6 * mm});
            skLineSegment(sketch, "E80", {"start": v(0, 104.25) * mm, "end": v(0, 74.25) * mm, "construction": true});
            skLineSegment(sketch, "E81", {"start": v(-33, 74.25) * mm, "end": v(-15, 92.25) * mm});
            skLineSegment(sketch, "E82", {"start": v(-15, 92.25) * mm, "end": v(-15, 104.25) * mm});
            skLineSegment(sketch, "E83", {"start": v(33, 74.25) * mm, "end": v(15, 92.25) * mm});
            skLineSegment(sketch, "E84", {"start": v(15, 92.25) * mm, "end": v(15, 104.25) * mm});
            skArc(sketch, "E85", {"start": v(15, 104.25) * mm, "mid": v(0, 119.25) * mm, "end": v(-15, 104.25) * mm});
            skLineSegment(sketch, "E86", {"start": v(-74.25, 0) * mm, "end": v(74.25, 0) * mm, "construction": true});
            skLineSegment(sketch, "E87.MirrorCS", {"start": v(33, -74.25) * mm, "end": v(15, -92.25) * mm});
            skCircle(sketch, "E88.MirrorC", {"center": v(0, -104.25) * mm, "radius": 6 * mm});
            skArc(sketch, "E89.MirrorCS", {"start": v(15, -104.25) * mm, "mid": v(0, -119.25) * mm, "end": v(-15, -104.25) * mm});
            skLineSegment(sketch, "E90.MirrorCS", {"start": v(0, -104.25) * mm, "end": v(0, -74.25) * mm, "construction": true});
            skLineSegment(sketch, "E91.MirrorCS", {"start": v(-33, -74.25) * mm, "end": v(-15, -92.25) * mm});
            skLineSegment(sketch, "E92.MirrorCS", {"start": v(15, -92.25) * mm, "end": v(15, -104.25) * mm});
            skLineSegment(sketch, "E93.MirrorCS", {"start": v(-15, -92.25) * mm, "end": v(-15, -104.25) * mm});
            skSolve(sketch);
        }
        {
            var Q0;
            Q0 = qSketchRegion(id + "F16", true);
            var Q1;
            Q1=makeQuery(id+"F2.opExtrude","CAP_FACE",FACE,{"disambiguationData":[OSD([sQuery(id+"F0.wireOp",EDGE,"E12"),sQuery(id+"F0.wireOp",EDGE,"E13"),sQuery(id+"F0.wireOp",EDGE,"E14"),sQuery(id+"F0.wireOp",EDGE,"E15"),sQuery(id+"F0.wireOp",EDGE,"E17.filletArc"),sQuery(id+"F0.wireOp",EDGE,"E18.filletArc"),sQuery(id+"F0.wireOp",EDGE,"E19.filletArc"),sQuery(id+"F0.wireOp",EDGE,"E20.filletArc"),sQuery(id+"F0.wireOp",EDGE,"E25.0"),sQuery(id+"F0.wireOp",EDGE,"E25.1"),sQuery(id+"F0.wireOp",EDGE,"E25.2"),sQuery(id+"F0.wireOp",EDGE,"E25.3"),sQuery(id+"F0.wireOp",EDGE,"E25.4"),sQuery(id+"F0.wireOp",EDGE,"E25.5"),sQuery(id+"F0.wireOp",EDGE,"E25.6"),sQuery(id+"F0.wireOp",EDGE,"E25.7")])],"isStart":false});
            extrude(context, id + "F17", {"entities" : qUnion([Q0]), "endBound" : BoundingType.UP_TO_SURFACE, "depth" : 25 * mm, "endBoundEntityFace" : qUnion([Q1]), "offsetDistance" : 25 * mm});
        }
    });
